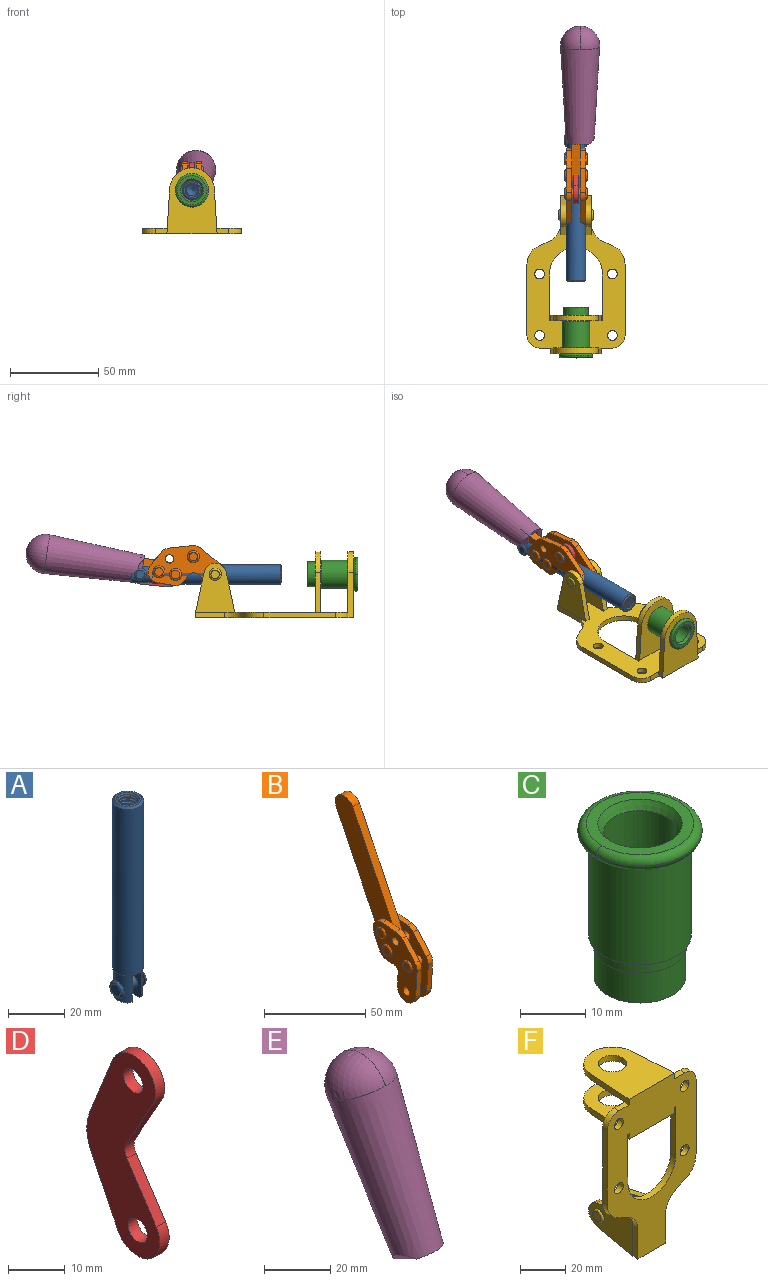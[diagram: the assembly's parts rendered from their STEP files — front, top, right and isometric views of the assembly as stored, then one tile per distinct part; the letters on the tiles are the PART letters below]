
ASSEMBLY  parts=6 mates=6
PART A: 48 faces, bbox 12.6x11.1x86.1 mm
  f0: torus R=2.41mm, axis (-1,0,0), area 15mm2, adj f30,f32,f34
  f1: torus R=2.41mm, axis (-1,0,0), area 15mm2, adj f29,f31,f33
  f2: cylinder r=5.54mm len=72.39mm, axis (0,0,1), area 2518.5mm2, adj f3,f4,f42,f43
  f3: cone r=5.54mm half-angle=45deg, axis (0,0,1), area 7.6mm2, adj f2,f5,f41
  f4: cone r=5.54mm half-angle=45deg, axis (0,0,-1), area 34.9mm2, adj f2,f39
  f5: cylinder r=5.08mm len=11.48mm, axis (0,0,1), area 108.3mm2, adj f3,f7,f8,f41
  f6: cylinder r=2.41mm len=4.83mm, axis (-1,0,0), area 71.2mm2, adj f40,f41
  f7: cylinder r=2.41mm len=4.83mm, axis (-1,0,0), area 7.6mm2, adj f5,f34
  f8: cone r=5.08mm half-angle=45deg, axis (0,0,1), area 10.6mm2, adj f5,f37,f41
  f9: cone r=3.98mm half-angle=45deg, axis (0,0,1), area 17.6mm2, adj f27,f39,f45,f46,f47
  f10: cylinder r=2.41mm len=4.83mm, axis (-1,0,0), area 7.6mm2, adj f33,f38
  f11: cylinder r=3.2mm len=6.4mm, axis (0,0,1), area 78.4mm2, adj f12,f28,f44,f45,f47
  f12: cylinder r=3.2mm len=6.4mm, axis (0,0,1), area 10.5mm2, adj f11,f13,f45,f47
  f13: cylinder r=3.2mm len=6.4mm, axis (0,0,1), area 10.5mm2, adj f12,f14,f45,f47
  f14: cylinder r=3.2mm len=6.4mm, axis (0,0,1), area 10.5mm2, adj f13,f15,f45,f47
  f15: cylinder r=3.2mm len=6.4mm, axis (0,0,1), area 10.5mm2, adj f14,f16,f45,f47
  f16: cylinder r=3.2mm len=6.4mm, axis (0,0,1), area 10.5mm2, adj f15,f17,f45,f47
  f17: cylinder r=3.2mm len=6.4mm, axis (0,0,1), area 10.5mm2, adj f16,f18,f45,f47
  f18: cylinder r=3.2mm len=6.4mm, axis (0,0,1), area 10.5mm2, adj f17,f19,f45,f47
  f19: cylinder r=3.2mm len=6.4mm, axis (0,0,1), area 10.5mm2, adj f18,f20,f45,f47
  f20: cylinder r=3.2mm len=6.4mm, axis (0,0,1), area 10.5mm2, adj f19,f21,f45,f47
  f21: cylinder r=3.2mm len=6.4mm, axis (0,0,1), area 10.5mm2, adj f20,f22,f45,f47
  f22: cylinder r=3.2mm len=6.4mm, axis (0,0,1), area 10.5mm2, adj f21,f23,f45,f47
  f23: cylinder r=3.2mm len=6.4mm, axis (0,0,1), area 10.5mm2, adj f22,f24,f45,f47
  f24: cylinder r=3.2mm len=6.4mm, axis (0,0,1), area 10.5mm2, adj f23,f25,f45,f47
  f25: cylinder r=3.2mm len=6.4mm, axis (0,0,1), area 10.5mm2, adj f24,f26,f45,f47
  f26: cylinder r=3.2mm len=6.4mm, axis (0,0,1), area 10.5mm2, adj f25,f27,f45,f47
  f27: cylinder r=3.2mm len=6.4mm, axis (0,0,1), area 7.4mm2, adj f9,f26,f45,f47
  f28: cone r=3.2mm half-angle=60deg, axis (0,0,1), area 37.2mm2, adj f11
  f29: plane 4.83x4.83mm, normal (-1,0,0), area 18.3mm2, adj f1,f31
  f30: plane 4.83x4.83mm, normal (1,0,0), area 18.3mm2, adj f0,f32
  f31: torus R=2.41mm, axis (-1,0,0), area 15mm2, adj f1,f29,f33
  f32: torus R=2.41mm, axis (-1,0,0), area 15mm2, adj f0,f30,f34
  f33: plane 6.83x6.83mm, normal (1,0,0), area 18.3mm2, adj f1,f10,f31
  f34: plane 6.83x6.83mm, normal (-1,0,0), area 18.3mm2, adj f0,f7,f32
  f35: cone r=5.08mm half-angle=45deg, axis (0,0,1), area 10.6mm2, adj f36,f38,f40
  f36: plane 7.25x1.97mm, normal (0,0,-1), area 10mm2, adj f35,f40
  f37: plane 7.25x1.97mm, normal (0,0,-1), area 10mm2, adj f8,f41
  f38: cylinder r=5.08mm len=11.48mm, axis (0,0,1), area 108.3mm2, adj f10,f35,f40,f42
  f39: plane 9.55x9.55mm, normal (0,0,1), area 22mm2, adj f4,f9
  f40: plane 12.76x10.09mm, normal (1,0,0), area 95.7mm2, adj f6,f35,f36,f38,f42,f43
  f41: plane 12.76x10.09mm, normal (-1,0,0), area 95.7mm2, adj f3,f5,f6,f8,f37,f43
  f42: cone r=5.54mm half-angle=45deg, axis (0,0,1), area 7.6mm2, adj f2,f38,f40
  f43: plane 11.07x4.7mm, normal (0,0,-1), area 50.4mm2, adj f2,f40,f41
  f44: plane 0.89x0.62mm, normal (-1,0,0), area 0.3mm2, adj f11,f45,f46,f47
  f45: bspline ~24.8x7.63mm, area 266.6mm2, adj f9,f11,f12,f13,f14,f15,f16,f17
  f46: bspline ~24.87x7.63mm, area 73.6mm2, adj f9,f44,f45,f47
  f47: bspline ~24.98x7.63mm, area 272.5mm2, adj f9,f11,f12,f13,f14,f15,f16,f17
PART B: 59 faces, bbox 12.9x60.2x99.6 mm
  f0: torus R=2.39mm, axis (-1,0,0), area 14.9mm2, adj f20,f43,f51
  f1: torus R=2.39mm, axis (-1,0,0), area 14.9mm2, adj f19,f42,f51
  f2: torus R=2.39mm, axis (-1,0,0), area 14.9mm2, adj f18,f35,f51
  f3: torus R=2.39mm, axis (-1,0,0), area 14.9mm2, adj f14,f17,f23
  f4: torus R=2.39mm, axis (-1,0,0), area 14.9mm2, adj f13,f16,f23
  f5: torus R=2.39mm, axis (-1,0,0), area 14.9mm2, adj f12,f15,f23
  f6: cylinder r=2.39mm len=4.78mm, axis (1,0,0), area 46.5mm2, adj f48,f50,f51
  f7: cylinder r=2.39mm len=4.78mm, axis (1,0,0), area 46.5mm2, adj f50,f51
  f8: cylinder r=6.35mm len=12.68mm, axis (1,0,0), area 61.8mm2, adj f38,f39,f50,f51
  f9: cylinder r=2.39mm len=4.78mm, axis (-1,0,0), area 70.5mm2, adj f46,f50
  f10: cylinder r=2.39mm len=4.78mm, axis (-1,0,0), area 46.5mm2, adj f23,f45,f46
  f11: cylinder r=2.39mm len=4.78mm, axis (-1,0,0), area 46.5mm2, adj f23,f46
  f12: plane 4.78x4.78mm, normal (1,0,0), area 17.9mm2, adj f5,f15
  f13: plane 4.78x4.78mm, normal (1,0,0), area 17.9mm2, adj f4,f16
  f14: plane 4.78x4.78mm, normal (1,0,0), area 17.9mm2, adj f3,f17
  f15: torus R=2.39mm, axis (-1,0,0), area 14.9mm2, adj f5,f12,f23
  f16: torus R=2.39mm, axis (-1,0,0), area 14.9mm2, adj f4,f13,f23
  f17: torus R=2.39mm, axis (-1,0,0), area 14.9mm2, adj f3,f14,f23
  f18: plane 4.78x4.78mm, normal (-1,0,0), area 17.9mm2, adj f2,f35
  f19: plane 4.78x4.78mm, normal (-1,0,0), area 17.9mm2, adj f1,f42
  f20: plane 4.78x4.78mm, normal (-1,0,0), area 17.9mm2, adj f0,f43
  f21: plane 2.26x0.2mm, normal (1,0,0), area 0.2mm2, adj f31,f44
  f22: plane 2.26x0.2mm, normal (-1,0,0), area 0.2mm2, adj f41,f44
  f23: plane 39.37x30.77mm, normal (1,0,0), area 565.5mm2, adj f3,f4,f5,f10,f11,f15,f16,f17
  f24: cylinder r=6.1mm len=4.15mm, axis (-1,0,0), area 14.7mm2, adj f23,f25,f32,f46
  f25: plane 10.25x9.01mm, normal (0,-0.75,0.66), area 42.3mm2, adj f23,f24,f26,f46
  f26: cylinder r=6.35mm len=4.64mm, axis (-1,0,0), area 15.6mm2, adj f23,f25,f27,f46
  f27: plane 15.84x3.1mm, normal (0,-1,-0.07), area 49.2mm2, adj f23,f26,f28,f46
  f28: cylinder r=6.35mm len=12.68mm, axis (-1,0,0), area 61.8mm2, adj f23,f27,f29,f46
  f29: plane 8.11x3.1mm, normal (0,1,0.07), area 25.2mm2, adj f23,f28,f30,f46
  f30: cylinder r=3.05mm len=3.25mm, axis (-1,0,0), area 14.8mm2, adj f23,f29,f31,f46
  f31: plane 5.99x3.1mm, normal (0,0.07,-1), area 18.6mm2, adj f21,f23,f30,f44,f46
  f32: plane 9.5x3.1mm, normal (0,-0.07,1), area 29.5mm2, adj f23,f24,f33,f46,f47
  f33: cylinder r=6.1mm len=8.63mm, axis (-1,0,0), area 39.1mm2, adj f23,f32,f34,f47
  f34: plane 8.65x3.96mm, normal (0,0.91,-0.42), area 29.5mm2, adj f23,f33,f44,f47
  f35: torus R=2.39mm, axis (-1,0,0), area 14.9mm2, adj f2,f18,f51
  f36: plane 10.25x9.01mm, normal (0,-0.75,0.66), area 42.3mm2, adj f37,f49,f50,f51
  f37: cylinder r=6.35mm len=4.64mm, axis (1,0,0), area 15.6mm2, adj f36,f38,f50,f51
  f38: plane 15.84x3.1mm, normal (0,-1,-0.07), area 49.2mm2, adj f8,f37,f50,f51
  f39: plane 8.11x3.1mm, normal (0,1,0.07), area 25.2mm2, adj f8,f40,f50,f51
  f40: cylinder r=3.05mm len=3.25mm, axis (1,0,0), area 14.8mm2, adj f39,f41,f50,f51
  f41: plane 5.99x3.1mm, normal (0,0.07,-1), area 18.6mm2, adj f22,f40,f44,f50,f51
  f42: torus R=2.39mm, axis (-1,0,0), area 14.9mm2, adj f1,f19,f51
  f43: torus R=2.39mm, axis (-1,0,0), area 14.9mm2, adj f0,f20,f51
  f44: cylinder r=6.35mm len=12.12mm, axis (-1,0,0), area 128.9mm2, adj f21,f22,f23,f31,f34,f41,f46,f47
  f45: plane 2.65x1.35mm, normal (1,0,0), area 1mm2, adj f10,f55
  f46: plane 39.08x20.42mm, normal (-1,0,0), area 412.5mm2, adj f9,f10,f11,f24,f25,f26,f27,f28
  f47: plane 77.62x39.82mm, normal (1,0,0), area 850mm2, adj f32,f33,f34,f44,f53,f54,f55
  f48: plane 2.65x1.35mm, normal (-1,0,0), area 1mm2, adj f6,f55
  f49: cylinder r=6.1mm len=4.15mm, axis (1,0,0), area 14.7mm2, adj f36,f50,f51,f56
  f50: plane 39.08x20.42mm, normal (1,0,0), area 412.5mm2, adj f6,f7,f8,f9,f36,f37,f38,f39
  f51: plane 39.37x30.77mm, normal (-1,0,0), area 565.5mm2, adj f0,f1,f2,f6,f7,f8,f35,f36
  f52: plane 8.65x3.96mm, normal (0,0.91,-0.42), area 29.5mm2, adj f44,f51,f57,f58
  f53: plane 68.49x33.4mm, normal (0,0.9,-0.44), area 358.1mm2, adj f44,f47,f54,f58
  f54: cylinder r=6.35mm len=12.06mm, axis (1,0,0), area 93.7mm2, adj f47,f53,f55,f58
  f55: plane 68.49x33.4mm, normal (0,-0.9,0.44), area 358.1mm2, adj f44,f45,f46,f47,f48,f50,f54,f58
  f56: plane 9.5x3.1mm, normal (0,-0.07,1), area 29.5mm2, adj f49,f50,f51,f57,f58
  f57: cylinder r=6.1mm len=8.63mm, axis (1,0,0), area 39.1mm2, adj f51,f52,f56,f58
  f58: plane 77.62x39.82mm, normal (-1,0,0), area 850mm2, adj f44,f52,f53,f54,f55,f56,f57
PART C: 15 faces, bbox 20.6x20.6x28.7 mm
  f0: torus R=8.26mm, axis (0,0,1), area 56.8mm2, adj f1,f10,f12
  f1: torus R=8.26mm, axis (0,0,1), area 56.8mm2, adj f0,f6,f13
  f2: cylinder r=5.59mm len=25.91mm, axis (0,0,1), area 909.6mm2, adj f3,f4
  f3: cone r=6.86mm half-angle=45deg, axis (0,0,-1), area 70.2mm2, adj f2,f14
  f4: cone r=6.47mm half-angle=30deg, axis (0,0,1), area 66.7mm2, adj f2,f13
  f5: cylinder r=7.04mm len=14.07mm, axis (0,0,1), area 252.6mm2, adj f11,f14
  f6: torus R=8.26mm, axis (0,0,1), area 56.8mm2, adj f1,f12,f13
  f7: cylinder r=7.16mm len=14.33mm, axis (0,0,1), area 91.5mm2, adj f9,f11
  f8: cylinder r=7.86mm len=18.42mm, axis (0,0,1), area 909.6mm2, adj f9,f10
  f9: plane 15.72x15.72mm, normal (0,0,-1), area 33mm2, adj f7,f8
  f10: plane 16.51x16.51mm, normal (0,0,-1), area 19.9mm2, adj f0,f8,f12
  f11: plane 14.33x14.33mm, normal (0,0,-1), area 5.7mm2, adj f5,f7
  f12: torus R=8.26mm, axis (0,0,1), area 56.8mm2, adj f0,f6,f10
  f13: plane 16.51x16.51mm, normal (0,0,1), area 82.7mm2, adj f1,f4,f6
  f14: plane 14.07x14.07mm, normal (0,0,-1), area 7.8mm2, adj f3,f5
PART D: 12 faces, bbox 2.3x18.2x42.8 mm
  f0: cylinder r=2.4mm len=4.8mm, axis (1,0,0), area 34.9mm2, adj f4,f11
  f1: cylinder r=10.41mm len=8.47mm, axis (1,0,0), area 20.2mm2, adj f4,f9,f10,f11
  f2: cylinder r=3.05mm len=3.16mm, axis (1,0,0), area 7.7mm2, adj f4,f6,f7,f11
  f3: cylinder r=2.4mm len=4.8mm, axis (1,0,0), area 34.9mm2, adj f4,f11
  f4: plane 42.81x18.23mm, normal (-1,0,0), area 414.1mm2, adj f0,f1,f2,f3,f5,f6,f7,f8
  f5: cylinder r=5.54mm len=10.67mm, axis (1,0,0), area 41.8mm2, adj f4,f6,f10,f11
  f6: plane 11.66x6.53mm, normal (0,-0.87,-0.49), area 30.9mm2, adj f2,f4,f5,f11
  f7: plane 11.17x7.33mm, normal (0,-0.84,0.55), area 30.9mm2, adj f2,f4,f8,f11
  f8: cylinder r=5.54mm len=10.51mm, axis (1,0,0), area 41.8mm2, adj f4,f7,f9,f11
  f9: plane 13.67x6.67mm, normal (0,0.9,-0.44), area 35.1mm2, adj f1,f4,f8,f11
  f10: plane 14.1x5.7mm, normal (0,0.93,0.37), area 35.1mm2, adj f1,f4,f5,f11
  f11: plane 42.81x18.23mm, normal (1,0,0), area 414.1mm2, adj f0,f1,f2,f3,f5,f6,f7,f8
PART E: 11 faces, bbox 22.3x42.6x64.5 mm
  f0: sphere r=11.13mm, area 411.4mm2, adj f1,f8
  f1: cone r=11.11mm half-angle=3.3deg, axis (0,0.44,0.9), area 3251.8mm2, adj f0,f7,f8,f9,f10
  f2: cylinder r=6.16mm len=11.7mm, axis (1,0,0), area 89.5mm2, adj f3,f4,f5,f6
  f3: plane 60.23x36.75mm, normal (-1,0,0), area 763.6mm2, adj f2,f4,f6,f10
  f4: plane 51.37x25.05mm, normal (0,0.9,-0.44), area 264.2mm2, adj f2,f3,f5,f10
  f5: plane 60.23x36.75mm, normal (1,0,0), area 763.6mm2, adj f2,f4,f6,f10
  f6: plane 51.37x25.05mm, normal (0,-0.9,0.44), area 264.2mm2, adj f2,f3,f5,f10
  f7: plane 9.95x5.95mm, normal (0.71,-0.31,-0.64), area 25.8mm2, adj f1,f10
  f8: sphere r=11.13mm, area 411.4mm2, adj f0,f1
  f9: plane 9.95x5.95mm, normal (-0.71,-0.31,-0.64), area 25.8mm2, adj f1,f10
  f10: plane 14.27x11.38mm, normal (0,-0.44,-0.9), area 106.7mm2, adj f1,f3,f4,f5,f6,f7,f9
PART F: 55 faces, bbox 55.7x37.4x89.8 mm
  f0: torus R=2.41mm, axis (-1,0,0), area 15mm2, adj f11,f15,f25
  f1: torus R=2.41mm, axis (-1,0,0), area 15mm2, adj f10,f12,f22
  f2: cylinder r=2.78mm len=5.56mm, axis (0,-1,0), area 54.2mm2, adj f30,f54
  f3: cylinder r=14.99mm len=29.97mm, axis (0,-1,0), area 145.9mm2, adj f30,f49,f53,f54
  f4: cylinder r=2.78mm len=5.56mm, axis (0,-1,0), area 54.2mm2, adj f30,f54
  f5: cylinder r=2.78mm len=5.56mm, axis (0,-1,0), area 54.2mm2, adj f30,f54
  f6: cylinder r=2.78mm len=5.56mm, axis (0,-1,0), area 54.2mm2, adj f30,f54
  f7: cylinder r=6.35mm len=12.7mm, axis (0,0,1), area 123.6mm2, adj f27,f51
  f8: cylinder r=6.35mm len=12.7mm, axis (0,0,-1), area 124.7mm2, adj f21,f35
  f9: cylinder r=2.41mm len=11.18mm, axis (-1,0,0), area 169.4mm2, adj f16,f19
  f10: plane 4.83x4.83mm, normal (1,0,0), area 18.3mm2, adj f1,f12
  f11: plane 4.83x4.83mm, normal (-1,0,0), area 18.3mm2, adj f0,f15
  f12: torus R=2.41mm, axis (-1,0,0), area 15mm2, adj f1,f10,f22
  f13: cylinder r=6.35mm len=12.41mm, axis (1,0,0), area 53.4mm2, adj f18,f19,f22,f23
  f14: cylinder r=6.35mm len=12.41mm, axis (-1,0,0), area 53.4mm2, adj f16,f17,f24,f25
  f15: torus R=2.41mm, axis (-1,0,0), area 15mm2, adj f0,f11,f25
  f16: plane 27.86x22.35mm, normal (1,0,0), area 425.4mm2, adj f9,f14,f17,f24,f30
  f17: plane 22.86x4.97mm, normal (0,0.21,0.98), area 72.5mm2, adj f14,f16,f25,f30
  f18: plane 22.86x4.97mm, normal (0,0.21,0.98), area 72.5mm2, adj f13,f19,f22,f30
  f19: plane 27.86x22.35mm, normal (-1,0,0), area 425.4mm2, adj f9,f13,f18,f23,f30
  f20: cylinder r=12.7mm len=25.35mm, axis (0,0,-1), area 119.8mm2, adj f21,f34,f35,f36
  f21: plane 34.21x28.07mm, normal (0,0,-1), area 702.4mm2, adj f8,f20,f30,f34,f36
  f22: plane 27.96x22.45mm, normal (1,0,0), area 407.2mm2, adj f1,f12,f13,f18,f23,f30,f42,f43
  f23: plane 22.86x4.97mm, normal (0,0.21,-0.98), area 72.5mm2, adj f13,f19,f22,f44
  f24: plane 22.86x4.97mm, normal (0,0.21,-0.98), area 72.5mm2, adj f14,f16,f25,f44
  f25: plane 27.86x22.35mm, normal (-1,0,0), area 407.1mm2, adj f0,f14,f15,f17,f24,f30,f45,f46
  f26: plane 3.1x0.95mm, normal (0,0,-1), area 2.7mm2, adj f30,f49,f50,f54
  f27: plane 34.21x28.07mm, normal (0,0,1), area 702.4mm2, adj f7,f28,f30,f50,f52
  f28: cylinder r=12.7mm len=25.35mm, axis (0,0,1), area 118.8mm2, adj f27,f50,f51,f52
  f29: plane 3.1x0.95mm, normal (0,0,-1), area 2.7mm2, adj f30,f52,f53,f54
  f30: plane 86.54x55.63mm, normal (0,1,0), area 2362.9mm2, adj f2,f3,f4,f5,f6,f16,f17,f18
  f31: plane 40.56x3.1mm, normal (-1,0,0), area 125.7mm2, adj f30,f32,f48,f54
  f32: cylinder r=7.11mm len=7.11mm, axis (0,-1,0), area 34.6mm2, adj f30,f31,f33,f54
  f33: plane 6.67x3.1mm, normal (0,0,1), area 20.4mm2, adj f30,f32,f34,f54
  f34: plane 25.39x3.13mm, normal (-1,0.06,0), area 79.5mm2, adj f20,f21,f33,f35,f54
  f35: plane 37.31x28.45mm, normal (0,0,1), area 789.9mm2, adj f8,f20,f34,f36,f54
  f36: plane 25.39x3.13mm, normal (1,0.06,0), area 79.5mm2, adj f20,f21,f35,f37,f54
  f37: plane 6.67x3.1mm, normal (0,0,1), area 20.4mm2, adj f30,f36,f38,f54
  f38: cylinder r=7.11mm len=7.11mm, axis (0,-1,0), area 34.6mm2, adj f30,f37,f39,f54
  f39: plane 40.56x3.1mm, normal (1,0,0), area 125.7mm2, adj f30,f38,f40,f54
  f40: cylinder r=11.18mm len=10.16mm, axis (0,-1,0), area 39.5mm2, adj f30,f39,f41,f54
  f41: plane 6.09x3.1mm, normal (0.42,0,-0.91), area 20.8mm2, adj f30,f40,f42,f54
  f42: cylinder r=11.18mm len=9.41mm, axis (0,-1,0), area 37.2mm2, adj f22,f30,f41,f43,f54
  f43: plane 16.5x3.1mm, normal (1,0,0), area 51.1mm2, adj f22,f42,f44,f54
  f44: plane 17.37x3.1mm, normal (0,0,-1), area 53.8mm2, adj f23,f24,f30,f43,f45,f54
  f45: plane 16.5x3.1mm, normal (-1,0,0), area 51.1mm2, adj f25,f44,f46,f54
  f46: cylinder r=11.18mm len=9.41mm, axis (0,-1,0), area 37.2mm2, adj f25,f30,f45,f47,f54
  f47: plane 6.09x3.1mm, normal (-0.42,0,-0.91), area 20.8mm2, adj f30,f46,f48,f54
  f48: cylinder r=11.18mm len=10.16mm, axis (0,-1,0), area 39.5mm2, adj f30,f31,f47,f54
  f49: plane 26.54x3.1mm, normal (-1,0,0), area 82.3mm2, adj f3,f26,f30,f54
  f50: plane 25.39x3.1mm, normal (1,0.06,0), area 78.8mm2, adj f26,f27,f28,f51,f54
  f51: plane 37.31x28.45mm, normal (0,0,-1), area 789.9mm2, adj f7,f28,f50,f52,f54
  f52: plane 25.39x3.1mm, normal (-1,0.06,0), area 78.8mm2, adj f27,f28,f29,f51,f54
  f53: plane 26.54x3.1mm, normal (1,0,0), area 82.3mm2, adj f3,f29,f30,f54
  f54: plane 89.66x55.63mm, normal (0,-1,0), area 2678.5mm2, adj f2,f3,f4,f5,f6,f26,f29,f31
PLACE A rot(axis=(1,0,0),90deg) t=(0,99.18,0)mm
PLACE B rot(axis=(-1,0,0),55deg) t=(0,53.4,63.18)mm
PLACE C rot(axis=(1,0,0),90deg) t=(0,9.14,0)mm
PLACE D rot(axis=(-1,0,0),106.3deg) t=(0,75.78,52.58)mm
PLACE E rot(axis=(-1,0,0),55deg) t=(2.31,53.4,63.18)mm
PLACE F rot(axis=(1,0,0),90deg) t=(0,9.14,0)mm fixed
MATE slider A.f2 <-> F.f7  axis (0,-1,0) through (0,40.4,24.61)mm
MATE revolute B.f7 <-> F.f0  axis (1,0,0) through (0,41.23,24.61)mm
MATE revolute D.f5 <-> A.f6  axis (1,0,0) through (0,83.71,24.61)mm
MATE revolute D.f3 <-> B.f4  axis (1,0,0) through (0,53.57,34.6)mm
MATE fastened C.f0 <-> F.f7  axis (0,1,0) through (0,-37.25,24.61)mm
MATE fastened E.f2 <-> B.f54  axis (1,0,0) through (0,139.02,36.41)mm
